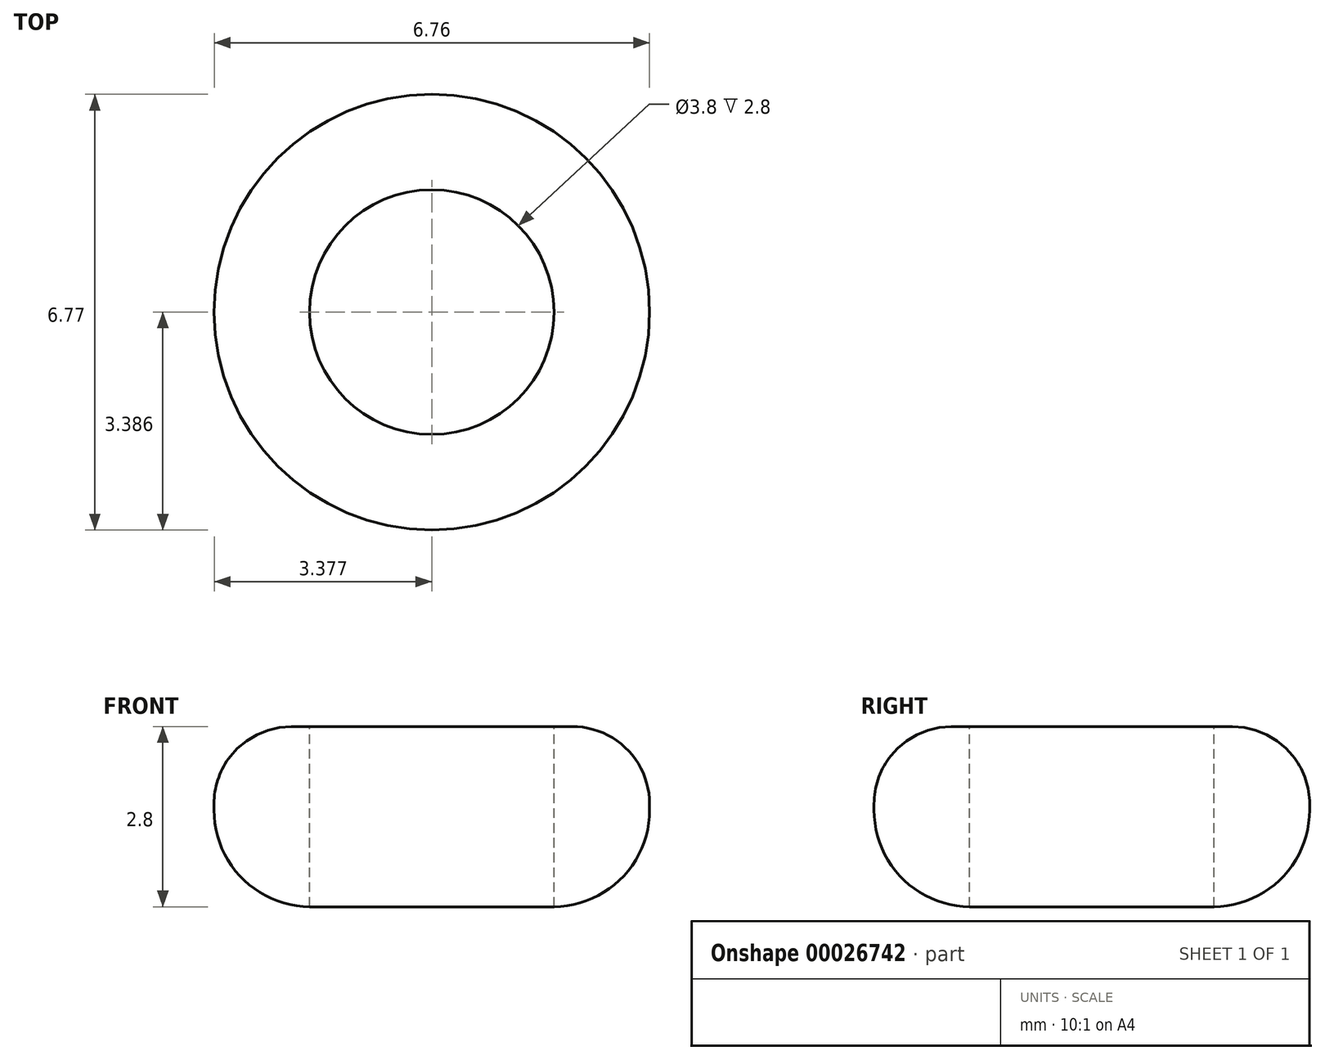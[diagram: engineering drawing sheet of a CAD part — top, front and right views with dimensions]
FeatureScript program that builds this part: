
annotation { "Feature Type Name" : "Feature", "Feature Type Description" : "" }
export const myFeature = defineFeature(function(context is Context, id is Id, definition is map)
    precondition{}
    {
        {
            var Q0;
            Q0=qCreatedBy(makeId("Top.planeOp"),FACE);
            var sketch = newSketch(context, id + "F0", { "sketchPlane" : qUnion([Q0])});
            skCircle(sketch, "E0", {"center": v(-12.51, 12.02) * mm, "radius": 3.38 * mm});
            skSolve(sketch);
        }
        {
            var Q0;
            Q0 = qSketchRegion(id + "F0", true);
            extrude(context, id + "F1", {"entities" : qUnion([Q0]), "depth" : 2.8 * mm});
        }
        {
            var Q0;
            Q0=makeQuery(id+"F1.opExtrude","CAP_FACE",FACE,{"disambiguationData":[OSD([sQuery(id+"F0.wireOp",EDGE,"E0")])],"isStart":false});
            var sketch = newSketch(context, id + "F2", { "sketchPlane" : qUnion([Q0])});
            skCircle(sketch, "E1", {"center": v(-12.51, 12.02) * mm, "radius": 1.9 * mm});
            skSolve(sketch);
        }
        {
            var Q0;
            Q0=makeQuery(id+"F2.imprint","IMPRINT",FACE,{"disambiguationData":[TD([[makeQuery(id+"F2.imprint","IMPRINT",EDGE,{"derivedFrom":sQuery(id+"F2.wireOp",EDGE,"E1")}),1.0]])]});
            extrude(context, id + "F3", {"entities" : qUnion([Q0]), "operationType" : NewBodyOperationType.REMOVE, "endBound" : BoundingType.THROUGH_ALL, "oppositeDirection" : true, "depth" : 25 * mm});
        }
        {
            var Q0;
            Q0=makeQuery(id+"F1.opExtrude","CAP_EDGE",EDGE,{"disambiguationData":[OSD([sQuery(id+"F0.wireOp",EDGE,"E0")])],"isStart":false});
            fillet(context, id + "F4", {"entities" : qUnion([Q0]), "radius" : 1.2 * mm, "tangentPropagation" : true, "allowEdgeOverflow" : false});
        }
        {
            var Q0;
            Q0=makeQuery(id+"F1.opExtrude","CAP_EDGE",EDGE,{"disambiguationData":[OSD([sQuery(id+"F0.wireOp",EDGE,"E0")])],"isStart":true});
            fillet(context, id + "F5", {"entities" : qUnion([Q0]), "radius" : 1.5 * mm, "tangentPropagation" : true, "allowEdgeOverflow" : false});
        }
    });
